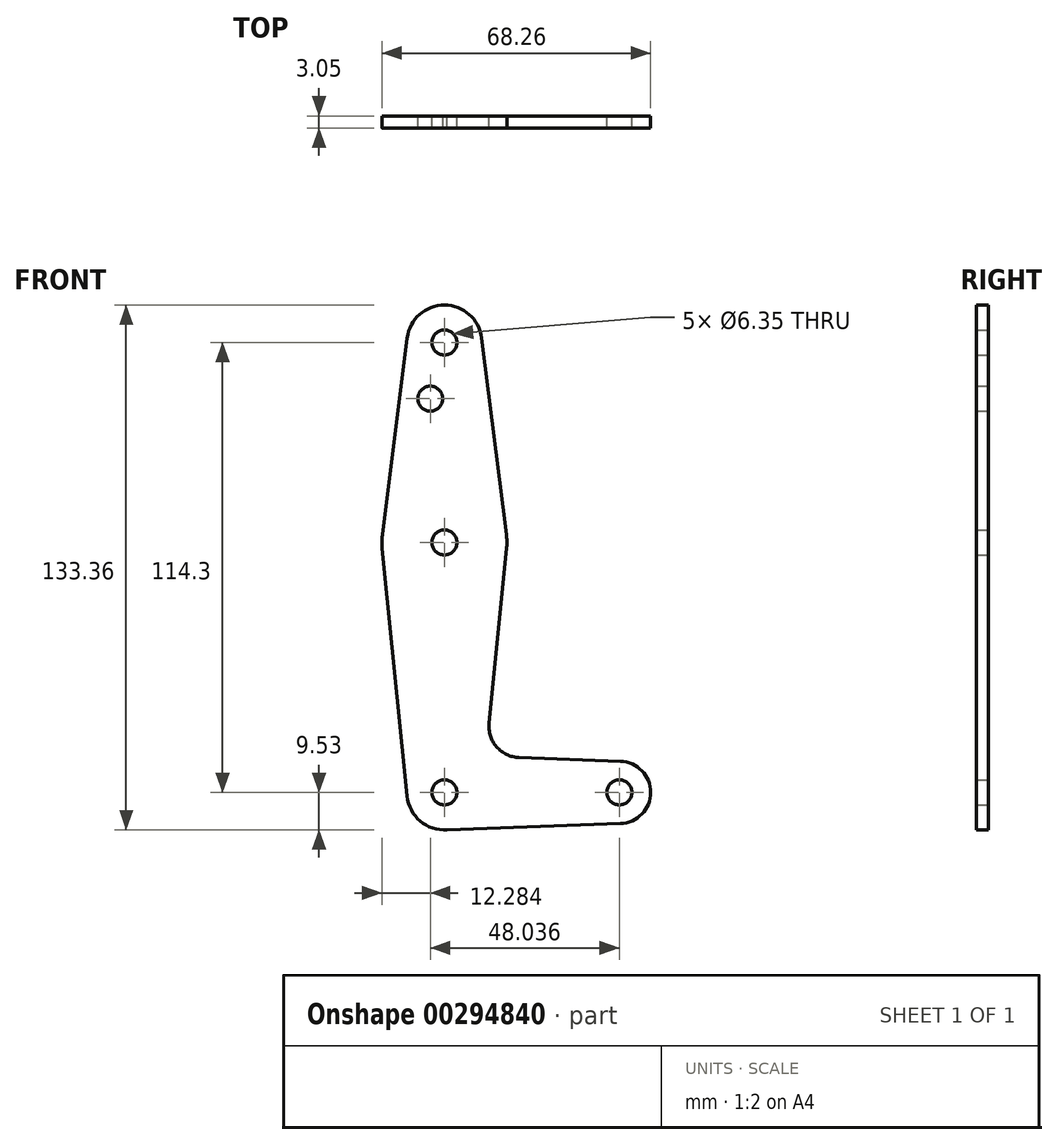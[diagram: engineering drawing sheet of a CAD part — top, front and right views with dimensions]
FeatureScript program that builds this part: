
annotation { "Feature Type Name" : "Feature", "Feature Type Description" : "" }
export const myFeature = defineFeature(function(context is Context, id is Id, definition is map)
    precondition{}
    {
        {
            var Q0;
            Q0=qCreatedBy(makeId("Front.planeOp"),FACE);
            var sketch = newSketch(context, id + "F0", { "sketchPlane" : qUnion([Q0])});
            skCircle(sketch, "E0", {"center": v(0, 0) * mm, "radius": 9.53 * mm});
            skCircle(sketch, "E1", {"center": v(44.45, 0) * mm, "radius": 7.94 * mm});
            skCircle(sketch, "E2", {"center": v(0, 63.5) * mm, "radius": 15.88 * mm});
            skCircle(sketch, "E3", {"center": v(0, 114.3) * mm, "radius": 9.53 * mm});
            skLineSegment(sketch, "E4", {"start": v(0, 114.3) * mm, "end": v(0, 63.5) * mm, "construction": true});
            skLineSegment(sketch, "E5", {"start": v(0, 63.5) * mm, "end": v(0, 0) * mm, "construction": true});
            skLineSegment(sketch, "E6", {"start": v(0, 0) * mm, "end": v(44.45, 0) * mm, "construction": true});
            skLineSegment(sketch, "E7", {"start": v(-9.45, 115.5) * mm, "end": v(-15.75, 65.48) * mm});
            skLineSegment(sketch, "E8", {"start": v(-15.8, 61.91) * mm, "end": v(-9.48, -0.95) * mm});
            skLineSegment(sketch, "E9", {"start": v(9.45, 115.5) * mm, "end": v(15.75, 65.48) * mm});
            skLineSegment(sketch, "E10", {"start": v(0, -9.53) * mm, "end": v(44.73, -7.93) * mm});
            skCircle(sketch, "E11", {"center": v(0, 114.3) * mm, "radius": 3.18 * mm});
            skCircle(sketch, "E12", {"center": v(0, 63.5) * mm, "radius": 3.18 * mm});
            skCircle(sketch, "E13", {"center": v(0, 0) * mm, "radius": 3.18 * mm});
            skCircle(sketch, "E14", {"center": v(44.45, 0) * mm, "radius": 3.18 * mm});
            skLineSegment(sketch, "E15", {"start": v(44.73, 7.93) * mm, "end": v(18.97, 8.85) * mm});
            skLineSegment(sketch, "E16", {"start": v(15.8, 61.91) * mm, "end": v(11.34, 17.6) * mm});
            skArc(sketch, "E17.filletArc", {"start": v(11.34, 17.6) * mm, "mid": v(13.26, 11.57) * mm, "end": v(18.97, 8.85) * mm});
            skCircle(sketch, "E18", {"center": v(-3.59, 100.03) * mm, "radius": 3.18 * mm});
            skSolve(sketch);
        }
        {
            var Q0;
            Q0 = qSketchRegion(id + "F0", true);
            extrude(context, id + "F1", {"entities" : qUnion([Q0]), "depth" : 3.05 * mm});
        }
    });
